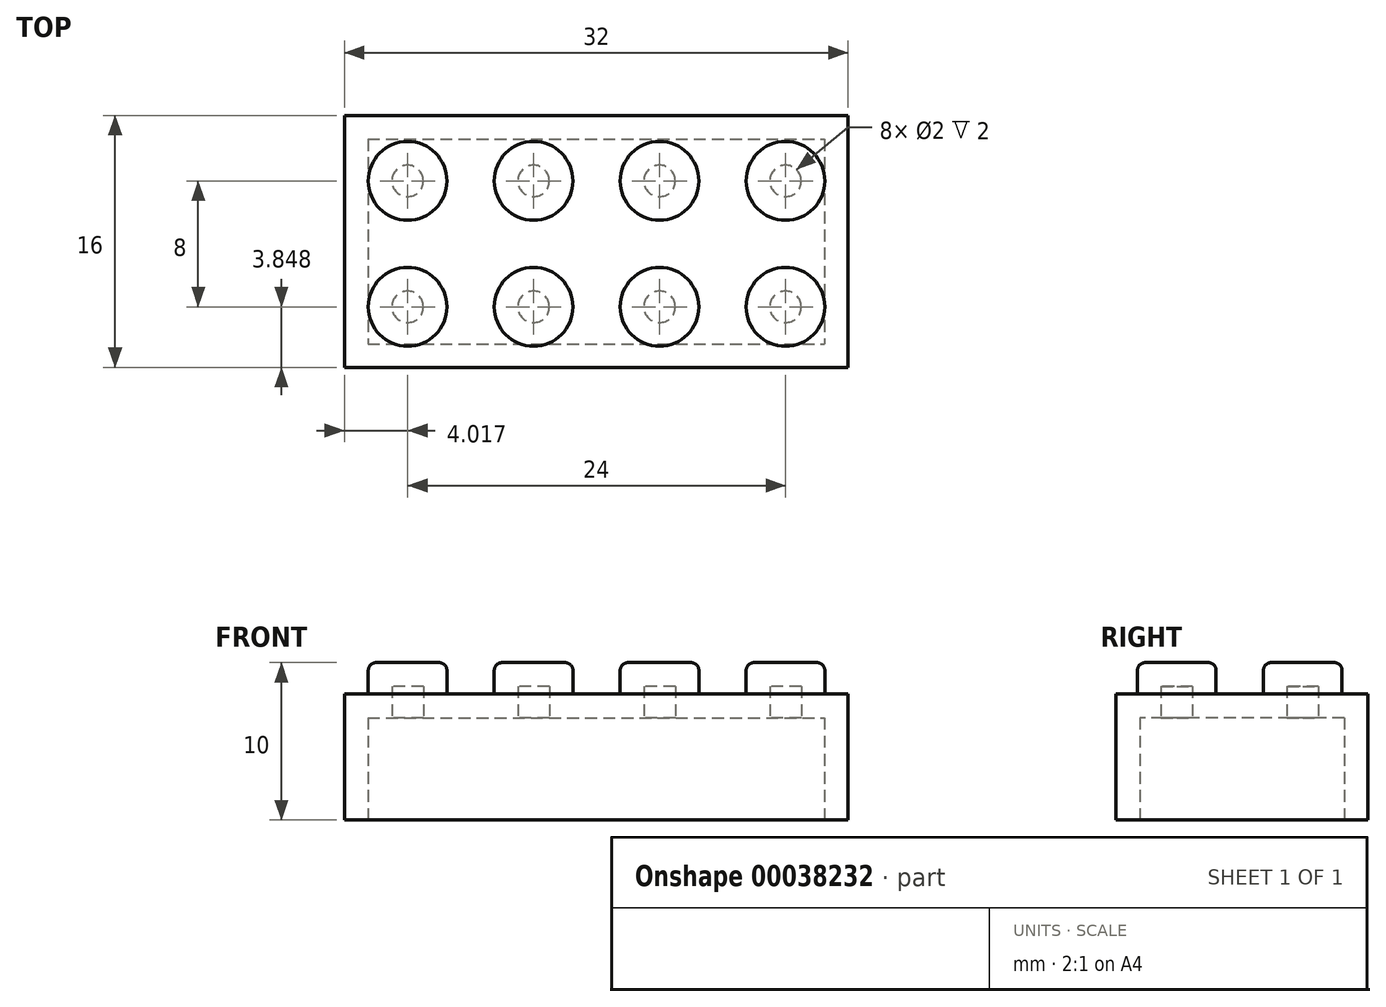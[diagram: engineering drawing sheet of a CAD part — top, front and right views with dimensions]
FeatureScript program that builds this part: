
annotation { "Feature Type Name" : "Feature", "Feature Type Description" : "" }
export const myFeature = defineFeature(function(context is Context, id is Id, definition is map)
    precondition{}
    {
        {
            var Q0;
            Q0=qCreatedBy(makeId("Top.planeOp"),FACE);
            var sketch = newSketch(context, id + "F0", { "sketchPlane" : qUnion([Q0])});
            skLineSegment(sketch, "E0.bottom", {"start": v(-10.58, 27.98) * mm, "end": v(21.42, 27.98) * mm});
            skLineSegment(sketch, "E0.top", {"start": v(-10.58, 11.98) * mm, "end": v(21.42, 11.98) * mm});
            skLineSegment(sketch, "E0.left", {"start": v(-10.58, 27.98) * mm, "end": v(-10.58, 11.98) * mm});
            skLineSegment(sketch, "E0.right", {"start": v(21.42, 27.98) * mm, "end": v(21.42, 11.98) * mm});
            skSolve(sketch);
        }
        {
            var Q0;
            Q0=makeQuery(id+"F0.imprint","IMPRINT",FACE,{"disambiguationData":[TD([[makeQuery(id+"F0.imprint","IMPRINT",EDGE,{"derivedFrom":sQuery(id+"F0.wireOp",EDGE,"E0.bottom")}),-1.0]])]});
            extrude(context, id + "F1", {"entities" : qUnion([Q0]), "depth" : 8 * mm});
        }
        {
            var Q0;
            Q0=qCreatedBy(makeId("Top.planeOp"),FACE);
            var sketch = newSketch(context, id + "F2", { "sketchPlane" : qUnion([Q0])});
            skPoint(sketch, "E1.endSnap0", {"position": v(-6.56, 19.83) * mm});
            skCircle(sketch, "E2", {"center": v(-6.56, 23.83) * mm, "radius": 2.5 * mm});
            skCircle(sketch, "E3", {"center": v(1.44, 23.83) * mm, "radius": 2.5 * mm});
            skCircle(sketch, "E4", {"center": v(9.44, 23.83) * mm, "radius": 2.5 * mm});
            skCircle(sketch, "E5", {"center": v(17.44, 23.83) * mm, "radius": 2.5 * mm});
            skCircle(sketch, "E6", {"center": v(17.44, 15.83) * mm, "radius": 2.5 * mm});
            skCircle(sketch, "E7", {"center": v(9.44, 15.83) * mm, "radius": 2.5 * mm});
            skCircle(sketch, "E8", {"center": v(1.44, 15.83) * mm, "radius": 2.5 * mm});
            skCircle(sketch, "E9", {"center": v(-6.56, 15.83) * mm, "radius": 2.5 * mm});
            skSolve(sketch);
        }
        {
            var Q0;
            Q0=makeQuery(id+"F2.imprint","IMPRINT",FACE,{"disambiguationData":[TD([[makeQuery(id+"F2.imprint","IMPRINT",EDGE,{"derivedFrom":sQuery(id+"F2.wireOp",EDGE,"E5")}),1.0]])]});
            var Q1;
            Q1=makeQuery(id+"F2.imprint","IMPRINT",FACE,{"disambiguationData":[TD([[makeQuery(id+"F2.imprint","IMPRINT",EDGE,{"derivedFrom":sQuery(id+"F2.wireOp",EDGE,"E4")}),1.0]])]});
            var Q2;
            Q2=makeQuery(id+"F2.imprint","IMPRINT",FACE,{"disambiguationData":[TD([[makeQuery(id+"F2.imprint","IMPRINT",EDGE,{"derivedFrom":sQuery(id+"F2.wireOp",EDGE,"E3")}),1.0]])]});
            var Q3;
            Q3=makeQuery(id+"F2.imprint","IMPRINT",FACE,{"disambiguationData":[TD([[makeQuery(id+"F2.imprint","IMPRINT",EDGE,{"derivedFrom":sQuery(id+"F2.wireOp",EDGE,"E2")}),1.0]])]});
            var Q4;
            Q4=makeQuery(id+"F2.imprint","IMPRINT",FACE,{"disambiguationData":[TD([[makeQuery(id+"F2.imprint","IMPRINT",EDGE,{"derivedFrom":sQuery(id+"F2.wireOp",EDGE,"E9")}),1.0]])]});
            var Q5;
            Q5=makeQuery(id+"F2.imprint","IMPRINT",FACE,{"disambiguationData":[TD([[makeQuery(id+"F2.imprint","IMPRINT",EDGE,{"derivedFrom":sQuery(id+"F2.wireOp",EDGE,"E8")}),1.0]])]});
            var Q6;
            Q6=makeQuery(id+"F2.imprint","IMPRINT",FACE,{"disambiguationData":[TD([[makeQuery(id+"F2.imprint","IMPRINT",EDGE,{"derivedFrom":sQuery(id+"F2.wireOp",EDGE,"E7")}),1.0]])]});
            var Q7;
            Q7=makeQuery(id+"F2.imprint","IMPRINT",FACE,{"disambiguationData":[TD([[makeQuery(id+"F2.imprint","IMPRINT",EDGE,{"derivedFrom":sQuery(id+"F2.wireOp",EDGE,"E6")}),1.0]])]});
            extrude(context, id + "F3", {"entities" : qUnion([Q0, Q1, Q2, Q3, Q4, Q5, Q6, Q7]), "operationType" : NewBodyOperationType.ADD, "depth" : 10 * mm});
        }
        {
            var Q0;
            Q0=makeQuery(id+"F3.opExtrude","CAP_FACE",FACE,{"disambiguationData":[OSD([sQuery(id+"F2.wireOp",EDGE,"E2")])],"isStart":false});
            var Q1;
            Q1=makeQuery(id+"F3.opExtrude","CAP_FACE",FACE,{"disambiguationData":[OSD([sQuery(id+"F2.wireOp",EDGE,"E9")])],"isStart":false});
            var Q2;
            Q2=makeQuery(id+"F3.opExtrude","CAP_FACE",FACE,{"disambiguationData":[OSD([sQuery(id+"F2.wireOp",EDGE,"E8")])],"isStart":false});
            var Q3;
            Q3=makeQuery(id+"F3.opExtrude","CAP_FACE",FACE,{"disambiguationData":[OSD([sQuery(id+"F2.wireOp",EDGE,"E3")])],"isStart":false});
            var Q4;
            Q4=makeQuery(id+"F3.opExtrude","CAP_FACE",FACE,{"disambiguationData":[OSD([sQuery(id+"F2.wireOp",EDGE,"E4")])],"isStart":false});
            var Q5;
            Q5=makeQuery(id+"F3.opExtrude","CAP_FACE",FACE,{"disambiguationData":[OSD([sQuery(id+"F2.wireOp",EDGE,"E5")])],"isStart":false});
            var Q6;
            Q6=makeQuery(id+"F3.opExtrude","CAP_FACE",FACE,{"disambiguationData":[OSD([sQuery(id+"F2.wireOp",EDGE,"E6")])],"isStart":false});
            var Q7;
            Q7=makeQuery(id+"F3.opExtrude","CAP_FACE",FACE,{"disambiguationData":[OSD([sQuery(id+"F2.wireOp",EDGE,"E7")])],"isStart":false});
            fillet(context, id + "F4", {"entities" : qUnion([Q0, Q1, Q2, Q3, Q4, Q5, Q6, Q7]), "radius" : 0.5 * mm, "tangentPropagation" : true, "allowEdgeOverflow" : false});
        }
        {
            var Q0;
            Q0=makeQuery(id+"F1.opExtrude","CAP_FACE",FACE,{"disambiguationData":[OSD([sQuery(id+"F0.wireOp",EDGE,"E0.bottom"),sQuery(id+"F0.wireOp",EDGE,"E0.top"),sQuery(id+"F0.wireOp",EDGE,"E0.left"),sQuery(id+"F0.wireOp",EDGE,"E0.right")])],"isStart":true});
            shell(context, id + "F5", {"entities" : qUnion([Q0]), "thickness" : 1.5 * mm});
        }
    });
